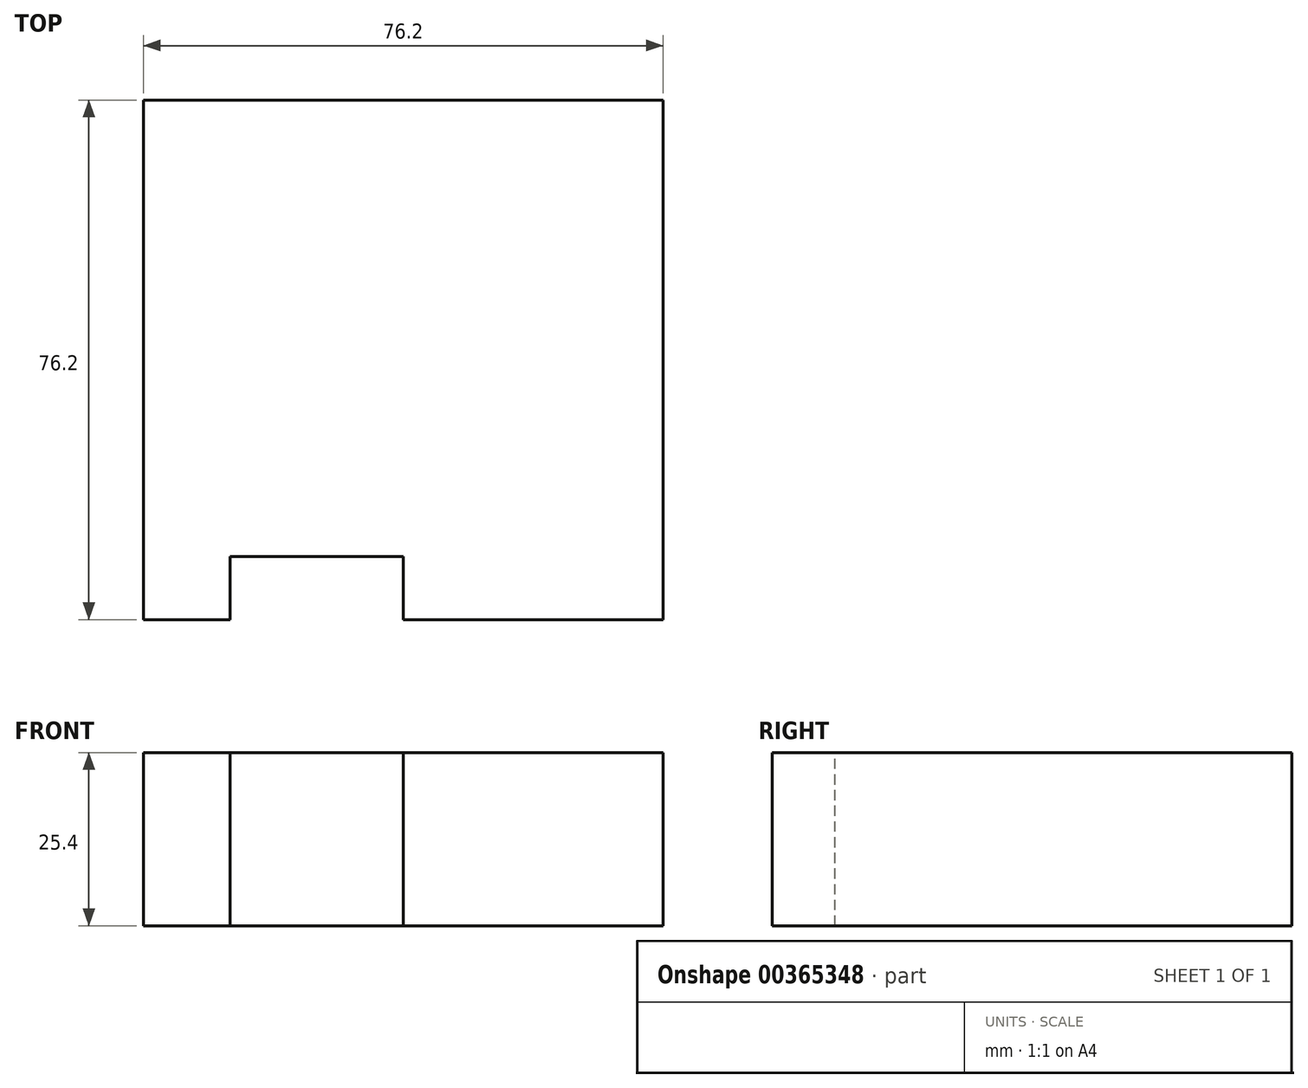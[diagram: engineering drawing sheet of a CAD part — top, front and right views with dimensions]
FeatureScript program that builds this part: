
annotation { "Feature Type Name" : "Feature", "Feature Type Description" : "" }
export const myFeature = defineFeature(function(context is Context, id is Id, definition is map)
    precondition{}
    {
        {
            var Q0;
            Q0=qCreatedBy(makeId("Top.planeOp"),FACE);
            var sketch = newSketch(context, id + "F0", { "sketchPlane" : qUnion([Q0])});
            skLineSegment(sketch, "E0.bottom", {"start": v(38.1, 38.1) * mm, "end": v(-38.1, 38.1) * mm});
            skLineSegment(sketch, "E0.top", {"start": v(38.1, -38.1) * mm, "end": v(-38.1, -38.1) * mm});
            skLineSegment(sketch, "E0.left", {"start": v(38.1, 38.1) * mm, "end": v(38.1, -38.1) * mm});
            skLineSegment(sketch, "E0.right", {"start": v(-38.1, 38.1) * mm, "end": v(-38.1, -38.1) * mm});
            skPoint(sketch, "E0.middle", {"position": v(0, 0) * mm});
            skSolve(sketch);
        }
        {
            var Q0;
            Q0 = qSketchRegion(id + "F0", true);
            extrude(context, id + "F1", {"entities" : qUnion([Q0]), "depth" : 25.4 * mm});
        }
        {
            var Q0;
            Q0=makeQuery(id+"F1.opExtrude","CAP_FACE",FACE,{"disambiguationData":[OSD([sQuery(id+"F0.wireOp",EDGE,"E0.bottom"),sQuery(id+"F0.wireOp",EDGE,"E0.top"),sQuery(id+"F0.wireOp",EDGE,"E0.left"),sQuery(id+"F0.wireOp",EDGE,"E0.right")])],"isStart":false});
            var sketch = newSketch(context, id + "F2", { "sketchPlane" : qUnion([Q0])});
            skSolve(sketch);
        }
        {
            var Q0;
            Q0=makeQuery(id+"F2.imprint","IMPRINT",FACE,{"disambiguationData":[TD([[makeQuery(id+"F2.imprint","IMPRINT",EDGE,{"derivedFrom":makeQuery(id+"F1.opExtrude","CAP_EDGE",EDGE,{"disambiguationData":[OSD([sQuery(id+"F0.wireOp",EDGE,"E0.bottom")])],"isStart":false})}),1.0]])]});
            var sketch = newSketch(context, id + "F3", { "sketchPlane" : qUnion([Q0])});
            skLineSegment(sketch, "E1", {"start": v(-25.4, -37.93) * mm, "end": v(-25.4, -28.87) * mm});
            skLineSegment(sketch, "E2", {"start": v(-25.4, -28.87) * mm, "end": v(0, -28.87) * mm});
            skLineSegment(sketch, "E3", {"start": v(0, -28.87) * mm, "end": v(0, -38.1) * mm});
            skLineSegment(sketch, "E4", {"start": v(-25.4, -37.93) * mm, "end": v(-25.4, -45.23) * mm});
            skLineSegment(sketch, "E5", {"start": v(-25.4, -45.23) * mm, "end": v(0, -45.23) * mm});
            skLineSegment(sketch, "E6", {"start": v(0, -45.23) * mm, "end": v(0, -38.1) * mm});
            skSolve(sketch);
        }
        {
            var Q0;
            Q0 = qSketchRegion(id + "F3", true);
            extrude(context, id + "F4", {"entities" : qUnion([Q0]), "operationType" : NewBodyOperationType.REMOVE, "oppositeDirection" : true, "depth" : 32.77 * mm});
        }
    });
